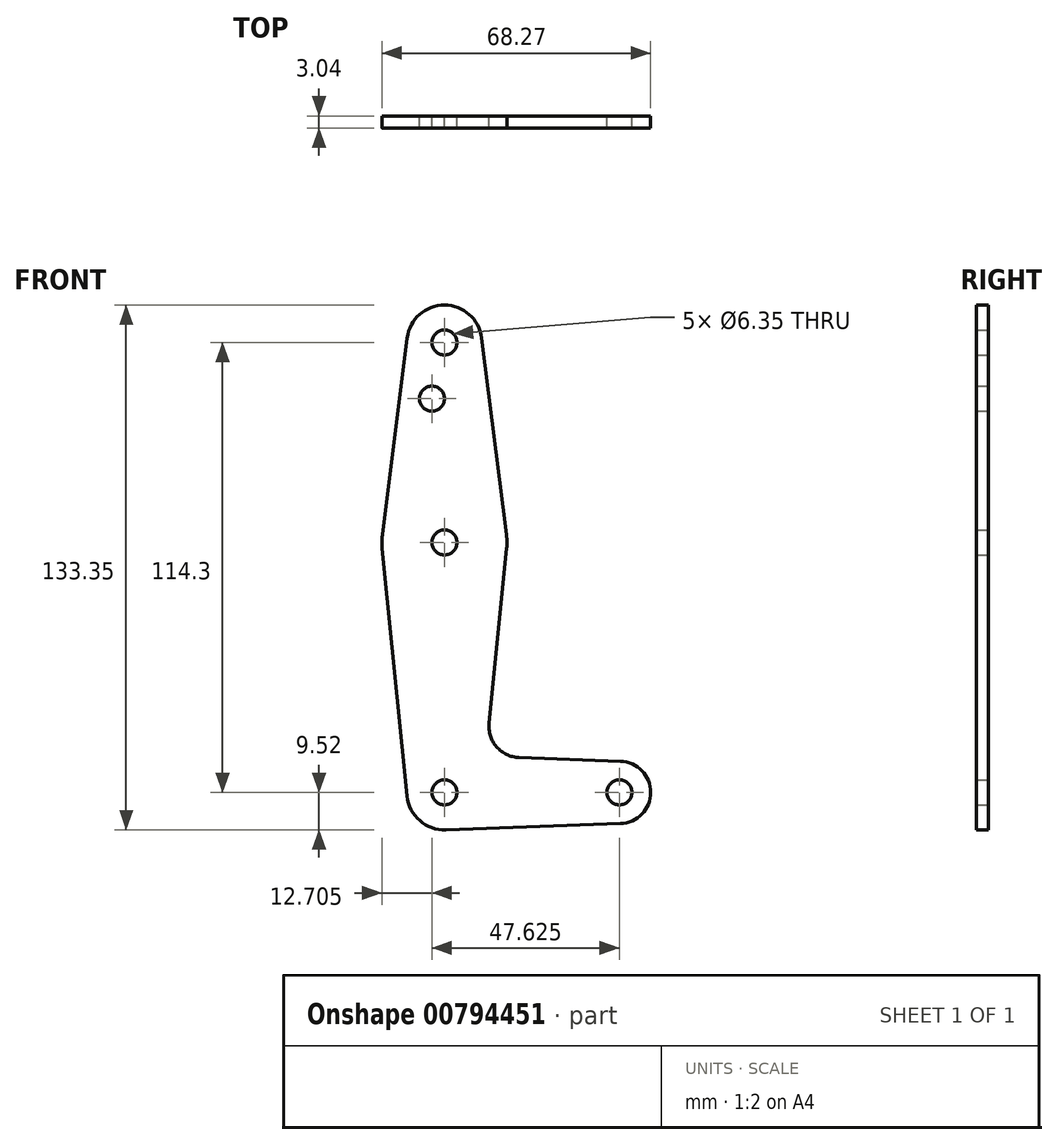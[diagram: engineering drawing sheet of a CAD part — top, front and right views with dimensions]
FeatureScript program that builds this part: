
annotation { "Feature Type Name" : "Feature", "Feature Type Description" : "" }
export const myFeature = defineFeature(function(context is Context, id is Id, definition is map)
    precondition{}
    {
        {
            var Q0;
            Q0=qCreatedBy(makeId("Front.planeOp"),FACE);
            var sketch = newSketch(context, id + "F0", { "sketchPlane" : qUnion([Q0])});
            skLineSegment(sketch, "E0", {"start": v(0, 114.3) * mm, "end": v(0, 0) * mm, "construction": true});
            skLineSegment(sketch, "E1", {"start": v(0, 0) * mm, "end": v(44.45, 0) * mm, "construction": true});
            skCircle(sketch, "E2", {"center": v(0, 0) * mm, "radius": 9.53 * mm});
            skCircle(sketch, "E3", {"center": v(44.45, 0) * mm, "radius": 7.94 * mm});
            skCircle(sketch, "E4", {"center": v(0, 114.3) * mm, "radius": 9.53 * mm});
            skCircle(sketch, "E5", {"center": v(0, 63.5) * mm, "radius": 15.88 * mm});
            skLineSegment(sketch, "E6", {"start": v(9.45, 115.5) * mm, "end": v(15.75, 65.48) * mm});
            skLineSegment(sketch, "E7", {"start": v(-9.45, 115.5) * mm, "end": v(-15.75, 65.48) * mm});
            skLineSegment(sketch, "E8", {"start": v(15.8, 61.91) * mm, "end": v(11.34, 17.6) * mm});
            skLineSegment(sketch, "E9", {"start": v(44.73, -7.93) * mm, "end": v(0, -9.53) * mm});
            skLineSegment(sketch, "E10", {"start": v(44.73, 7.93) * mm, "end": v(18.97, 8.85) * mm});
            skCircle(sketch, "E11", {"center": v(0, 114.3) * mm, "radius": 3.18 * mm});
            skCircle(sketch, "E12", {"center": v(0, 63.5) * mm, "radius": 3.18 * mm});
            skCircle(sketch, "E13", {"center": v(0, 0) * mm, "radius": 3.18 * mm});
            skCircle(sketch, "E14", {"center": v(44.45, 0) * mm, "radius": 3.18 * mm});
            skCircle(sketch, "E15", {"center": v(-3.17, 100.03) * mm, "radius": 3.18 * mm});
            skPoint(sketch, "E16.newPointA", {"position": v(0, 9.53) * mm});
            skArc(sketch, "E16.filletArc", {"start": v(11.34, 17.6) * mm, "mid": v(13.26, 11.57) * mm, "end": v(18.97, 8.85) * mm});
            skLineSegment(sketch, "E17", {"start": v(-15.8, 61.91) * mm, "end": v(-9.48, -0.95) * mm});
            skSolve(sketch);
        }
        {
            var Q0;
            Q0 = qSketchRegion(id + "F0", true);
            var Q1;
            Q1=sQuery(id+"F0.wireOp",EDGE,"E7");
            var Q2;
            Q2=sQuery(id+"F0.wireOp",EDGE,"E17");
            extrude(context, id + "F1", {"entities" : qUnion([Q0]), "surfaceEntities" : qUnion([Q1, Q2]), "endBound" : BoundingType.SYMMETRIC, "depth" : 3.05 * mm, "offsetDistance" : 25.4 * mm});
        }
    });
